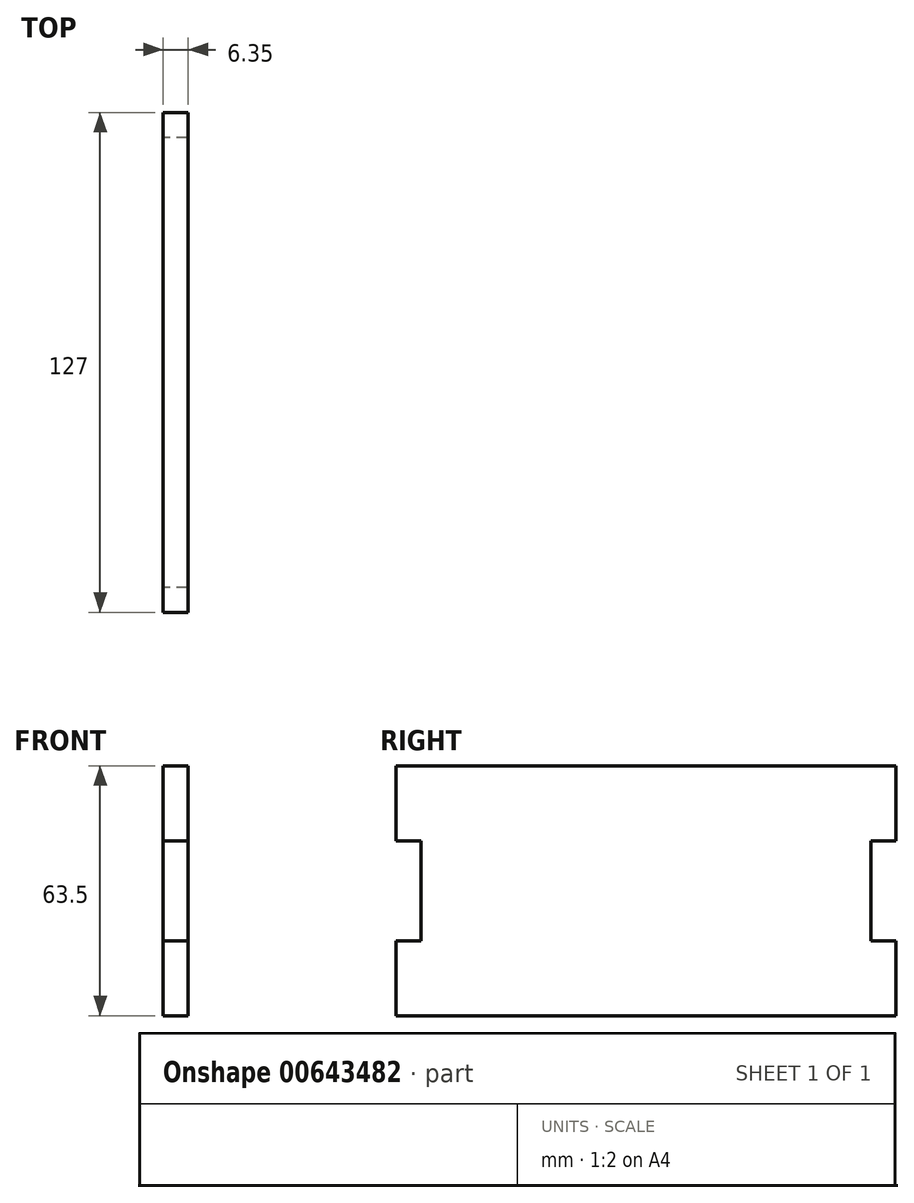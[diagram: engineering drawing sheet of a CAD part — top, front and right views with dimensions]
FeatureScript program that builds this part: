
annotation { "Feature Type Name" : "Feature", "Feature Type Description" : "" }
export const myFeature = defineFeature(function(context is Context, id is Id, definition is map)
    precondition{}
    {
        {
            var Q0;
            Q0=qCreatedBy(makeId("Right.planeOp"),FACE);
            var sketch = newSketch(context, id + "F0", { "sketchPlane" : qUnion([Q0])});
            skLineSegment(sketch, "E0.bottom", {"start": v(-38.9, 24.18) * mm, "end": v(88.1, 24.18) * mm});
            skLineSegment(sketch, "E0.top", {"start": v(-38.9, -39.32) * mm, "end": v(88.1, -39.32) * mm});
            skLineSegment(sketch, "E0.left", {"start": v(-38.9, 24.18) * mm, "end": v(-38.9, -39.32) * mm});
            skLineSegment(sketch, "E0.right", {"start": v(88.1, 24.18) * mm, "end": v(88.1, -39.32) * mm});
            skLineSegment(sketch, "E1.bottom", {"start": v(-0.8, 24.18) * mm, "end": v(50, 24.18) * mm});
            skLineSegment(sketch, "E1.top", {"start": v(-0.8, 30.53) * mm, "end": v(50, 30.53) * mm});
            skLineSegment(sketch, "E1.left", {"start": v(-0.8, 24.18) * mm, "end": v(-0.8, 30.53) * mm});
            skLineSegment(sketch, "E1.right", {"start": v(50, 24.18) * mm, "end": v(50, 30.53) * mm});
            skLineSegment(sketch, "E2.bottom", {"start": v(-0.8, -39.32) * mm, "end": v(50, -39.32) * mm});
            skLineSegment(sketch, "E2.top", {"start": v(-0.8, -45.67) * mm, "end": v(50, -45.67) * mm});
            skLineSegment(sketch, "E2.left", {"start": v(-0.8, -39.32) * mm, "end": v(-0.8, -45.67) * mm});
            skLineSegment(sketch, "E2.right", {"start": v(50, -39.32) * mm, "end": v(50, -45.67) * mm});
            skLineSegment(sketch, "E3.bottom", {"start": v(88.1, 5.13) * mm, "end": v(81.75, 5.13) * mm});
            skLineSegment(sketch, "E3.top", {"start": v(88.1, -20.27) * mm, "end": v(81.75, -20.27) * mm});
            skLineSegment(sketch, "E3.left", {"start": v(88.1, 5.13) * mm, "end": v(88.1, -20.27) * mm});
            skLineSegment(sketch, "E3.right", {"start": v(81.75, 5.13) * mm, "end": v(81.75, -20.27) * mm});
            skLineSegment(sketch, "E4.bottom", {"start": v(-38.9, 5.13) * mm, "end": v(-32.55, 5.13) * mm});
            skLineSegment(sketch, "E4.top", {"start": v(-38.9, -20.27) * mm, "end": v(-32.55, -20.27) * mm});
            skLineSegment(sketch, "E4.left", {"start": v(-38.9, 5.13) * mm, "end": v(-38.9, -20.27) * mm});
            skLineSegment(sketch, "E4.right", {"start": v(-32.55, 5.13) * mm, "end": v(-32.55, -20.27) * mm});
            skSolve(sketch);
        }
        {
            var Q0;
            {var subQ3=sQuery(id+"F0.wireOp",EDGE,"E0.left");Q0=makeQuery(id+"F0.imprint","IMPRINT",FACE,{"disambiguationData":[TD([[makeQuery(id+"F0.imprint","IMPRINT",EDGE,{"derivedFrom":subQ3}),1.0]])]});}
            var Q1;
            Q1=makeQuery(id+"F0.imprint","IMPRINT",FACE,{"disambiguationData":[TD([[makeQuery(id+"F0.imprint","IMPRINT",EDGE,{"derivedFrom":sQuery(id+"F0.wireOp",EDGE,"E1.bottom")}),1.0]])]});
            var Q2;
            Q2=makeQuery(id+"F0.imprint","IMPRINT",FACE,{"disambiguationData":[TD([[makeQuery(id+"F0.imprint","IMPRINT",EDGE,{"derivedFrom":sQuery(id+"F0.wireOp",EDGE,"E2.bottom")}),-1.0]])]});
            extrude(context, id + "F1", {"entities" : qUnion([Q0, Q1, Q2]), "depth" : 6.35 * mm, "offsetDistance" : 25.4 * mm});
        }
    });
